# Revit family: Gira_213800
name_source: partatom
category: Electrical Fixtures
revit_build: Autodesk Revit 2017 (Build: 20160225_1515(x64)
units: mm (PartAtom-declared; Revit-internal decimal feet)

## family parameters
Cut with Voids When Loaded = No
Host = Face
Maintain Annotation Orientation = No
Part Type = Normal
Room Calculation Point = No
Round Connector Dimension = Use Diameter
Shared = No

## types (1)
- Pow.supply 1280 mA choke KNX DRA
    BIM = https://media.live.bim.site 00_REG 6.rfa
    BIMSITE_PRODUCT_ID = d2853a5bf78b8d7a9cae491f6953783b0369dc1b
    Cost = 0 $
    Default Elevation = 1219 mm
    Description = PS 1280mA choke DRA KNX KNX power supply 1280 mA with integrated choke, Power supplies for supplying KNX devices with bus voltage.,Features: - Output with integrated choke to supply KNX bus lines. - Output DC 30 V to supply additional devices. - Rated current can be flexibly split up amongst outputs. - Reset button. - Short-circuit-proof. - Overvoltage protection. - Open circuit-proof. - Suitable for operation in systems with emergency power supply. - Isolated signal contact for operating message and diagnostic message.,Notes : - Installation on DIN top-hat rail. - VDE approval in accordance with EN 60669-1, EN 60669-2-1.
    GTIN = 4010337023241
    HAN = 213800
    HeinzeBIM = https://www.heinze.de
    Manufacturer = Gira
    URL = https://www.gira.de

## geometry (parser evidence)
native form markers: Blend x2, Sweep x3
no freeform markers — native parametric forms only
